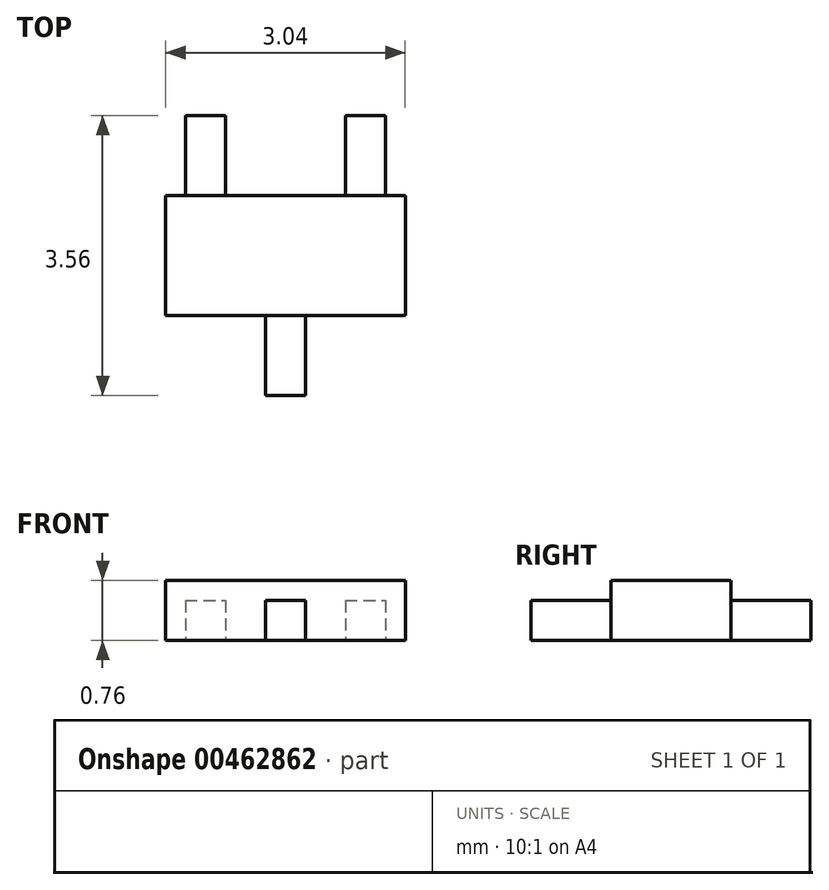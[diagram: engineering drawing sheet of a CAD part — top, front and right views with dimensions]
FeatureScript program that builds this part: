
annotation { "Feature Type Name" : "Feature", "Feature Type Description" : "" }
export const myFeature = defineFeature(function(context is Context, id is Id, definition is map)
    precondition{}
    {
        {
            var Q0;
            Q0=qCreatedBy(makeId("Top.planeOp"),FACE);
            var sketch = newSketch(context, id + "F0", { "sketchPlane" : qUnion([Q0])});
            skLineSegment(sketch, "E0.bottom", {"start": v(-1.52, 0.76) * mm, "end": v(1.52, 0.76) * mm});
            skLineSegment(sketch, "E0.top", {"start": v(-1.52, -0.76) * mm, "end": v(1.52, -0.76) * mm});
            skLineSegment(sketch, "E0.left", {"start": v(-1.52, 0.76) * mm, "end": v(-1.52, -0.76) * mm});
            skLineSegment(sketch, "E0.right", {"start": v(1.52, 0.76) * mm, "end": v(1.52, -0.76) * mm});
            skPoint(sketch, "E0.middle", {"position": v(0, 0) * mm});
            skLineSegment(sketch, "E1.bottom", {"start": v(-0.25, -0.76) * mm, "end": v(0.25, -0.76) * mm});
            skLineSegment(sketch, "E1.top", {"start": v(-0.25, -1.78) * mm, "end": v(0.25, -1.78) * mm});
            skLineSegment(sketch, "E1.left", {"start": v(-0.25, -0.76) * mm, "end": v(-0.25, -1.78) * mm});
            skLineSegment(sketch, "E1.right", {"start": v(0.25, -0.76) * mm, "end": v(0.25, -1.78) * mm});
            skPoint(sketch, "E1.middle", {"position": v(0, -1.27) * mm});
            skPoint(sketch, "E1.middle.positionSnap0", {"position": v(0, -0.76) * mm});
            skPoint(sketch, "E1.centerSnap0", {"position": v(0, -0.76) * mm});
            skLineSegment(sketch, "E2.bottom", {"start": v(-1.27, 1.78) * mm, "end": v(-0.76, 1.78) * mm});
            skLineSegment(sketch, "E2.top", {"start": v(-1.27, 0.76) * mm, "end": v(-0.76, 0.76) * mm});
            skLineSegment(sketch, "E2.left", {"start": v(-1.27, 1.78) * mm, "end": v(-1.27, 0.76) * mm});
            skLineSegment(sketch, "E2.right", {"start": v(-0.76, 1.78) * mm, "end": v(-0.76, 0.76) * mm});
            skPoint(sketch, "E2.middle", {"position": v(-1.02, 1.27) * mm});
            skLineSegment(sketch, "E3.bottom", {"start": v(0.76, 1.78) * mm, "end": v(1.27, 1.78) * mm});
            skLineSegment(sketch, "E3.top", {"start": v(0.76, 0.76) * mm, "end": v(1.27, 0.76) * mm});
            skLineSegment(sketch, "E3.left", {"start": v(0.76, 1.78) * mm, "end": v(0.76, 0.76) * mm});
            skLineSegment(sketch, "E3.right", {"start": v(1.27, 1.78) * mm, "end": v(1.27, 0.76) * mm});
            skPoint(sketch, "E3.middle", {"position": v(1.02, 1.27) * mm});
            skSolve(sketch);
        }
        {
            var Q0;
            Q0 = qSketchRegion(id + "F0", true);
            extrude(context, id + "F1", {"entities" : qUnion([Q0]), "depth" : 0.76 * mm, "offsetDistance" : 25.4 * mm});
        }
        {
            var Q0;
            Q0=makeQuery(id+"F1.opExtrude","CAP_FACE",FACE,{"disambiguationData":[OSD([sQuery(id+"F0.wireOp",EDGE,"E0.bottom"),sQuery(id+"F0.wireOp",EDGE,"E0.top"),sQuery(id+"F0.wireOp",EDGE,"E0.left"),sQuery(id+"F0.wireOp",EDGE,"E0.right"),sQuery(id+"F0.wireOp",EDGE,"E1.top"),sQuery(id+"F0.wireOp",EDGE,"E1.left"),sQuery(id+"F0.wireOp",EDGE,"E1.right"),sQuery(id+"F0.wireOp",EDGE,"E2.bottom"),sQuery(id+"F0.wireOp",EDGE,"E2.left"),sQuery(id+"F0.wireOp",EDGE,"E2.right"),sQuery(id+"F0.wireOp",EDGE,"E3.bottom"),sQuery(id+"F0.wireOp",EDGE,"E3.left"),sQuery(id+"F0.wireOp",EDGE,"E3.right")])],"isStart":false});
            var sketch = newSketch(context, id + "F2", { "sketchPlane" : qUnion([Q0])});
            skLineSegment(sketch, "E4.bottom", {"start": v(-1.52, 0.76) * mm, "end": v(1.52, 0.76) * mm});
            skLineSegment(sketch, "E4.top", {"start": v(-1.52, -0.76) * mm, "end": v(1.52, -0.76) * mm});
            skLineSegment(sketch, "E4.left", {"start": v(-1.52, 0.76) * mm, "end": v(-1.52, -0.76) * mm});
            skLineSegment(sketch, "E4.right", {"start": v(1.52, 0.76) * mm, "end": v(1.52, -0.76) * mm});
            skPoint(sketch, "E4.middle", {"position": v(0, 0) * mm});
            skLineSegment(sketch, "E5.bottom", {"start": v(-2.59, 2.09) * mm, "end": v(2.59, 2.09) * mm});
            skLineSegment(sketch, "E5.top", {"start": v(-2.59, -2.09) * mm, "end": v(2.59, -2.09) * mm});
            skLineSegment(sketch, "E5.left", {"start": v(-2.59, 2.09) * mm, "end": v(-2.59, -2.09) * mm});
            skLineSegment(sketch, "E5.right", {"start": v(2.59, 2.09) * mm, "end": v(2.59, -2.09) * mm});
            skSolve(sketch);
        }
        {
            var Q0;
            Q0 = qSketchRegion(id + "F2", true);
            extrude(context, id + "F3", {"entities" : qUnion([Q0]), "operationType" : NewBodyOperationType.REMOVE, "oppositeDirection" : true, "depth" : 0.25 * mm, "offsetDistance" : 25.4 * mm});
        }
    });
